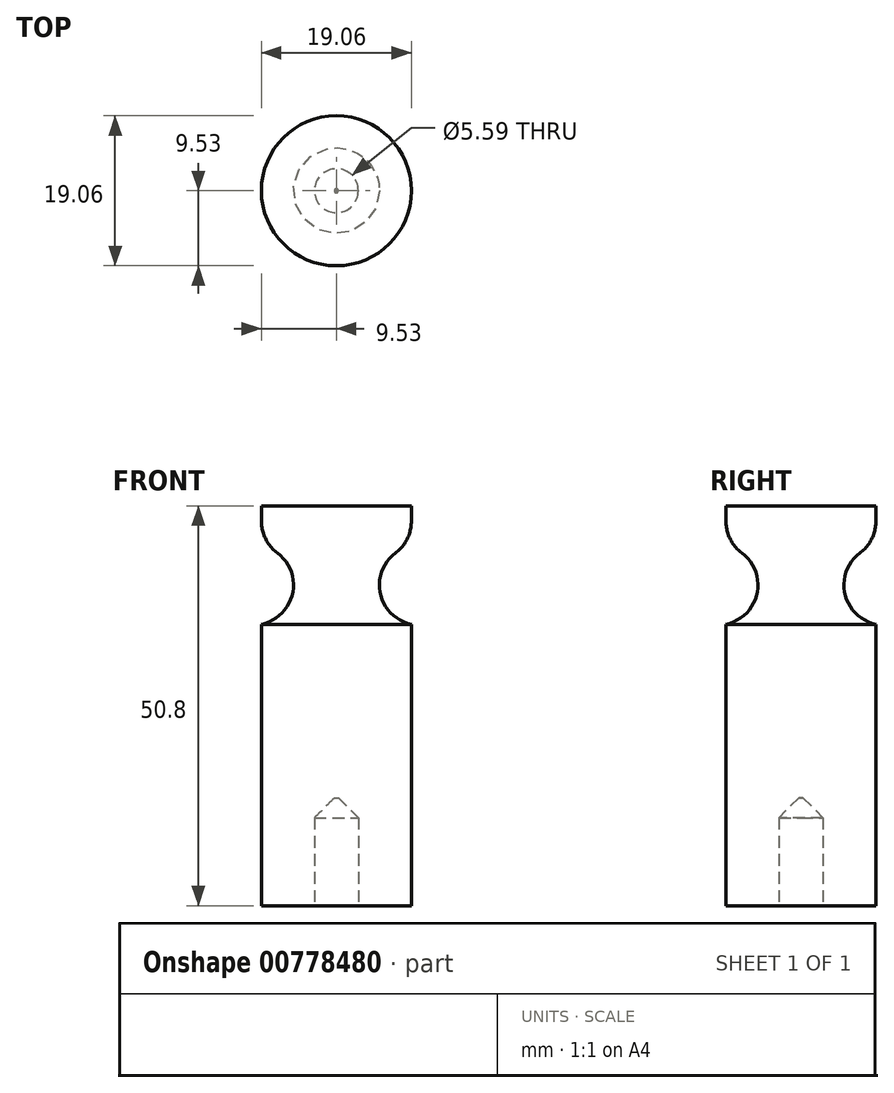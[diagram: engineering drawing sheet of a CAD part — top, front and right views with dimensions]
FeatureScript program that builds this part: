
annotation { "Feature Type Name" : "Feature", "Feature Type Description" : "" }
export const myFeature = defineFeature(function(context is Context, id is Id, definition is map)
    precondition{}
    {
        {
            var Q0;
            Q0=qCreatedBy(makeId("Top.planeOp"),FACE);
            var sketch = newSketch(context, id + "F0", { "sketchPlane" : qUnion([Q0])});
            skCircle(sketch, "E0", {"center": v(0, 0) * mm, "radius": 9.53 * mm});
            skSolve(sketch);
        }
        {
            var Q0;
            Q0 = qSketchRegion(id + "F0", true);
            extrude(context, id + "F1", {"entities" : qUnion([Q0]), "depth" : 50.8 * mm, "offsetDistance" : 25.4 * mm});
        }
        {
            var Q0;
            Q0=qCreatedBy(makeId("Front.planeOp"),FACE);
            var sketch = newSketch(context, id + "F2", { "sketchPlane" : qUnion([Q0])});
            skArc(sketch, "E1", {"start": v(9.52, 45.72) * mm, "mid": v(5.46, 40.74) * mm, "end": v(9.53, 35.76) * mm});
            skLineSegment(sketch, "E2", {"start": v(9.52, 45.72) * mm, "end": v(9.53, 35.76) * mm});
            skLineSegment(sketch, "E3", {"start": v(0, 50.97) * mm, "end": v(0, -98.87) * mm});
            skSolve(sketch);
        }
        {
            var Q0;
            Q0 = qSketchRegion(id + "F2", true);
            var Q1;
            Q1=sQuery(id+"F2.wireOp",EDGE,"E3");
            revolve(context, id + "F3", {"operationType" : NewBodyOperationType.REMOVE, "surfaceOperationType" : NewSurfaceOperationType.NEW, "entities" : qUnion([Q0]), "axis" : qUnion([Q1]), "revolveType" : RevolveType.FULL});
        }
        {
            var Q0;
            {var subQ0=sQuery(id+"F2.wireOp",EDGE,"E2");var subQ1=sQuery(id+"F2.wireOp",EDGE,"E1");Q0=makeQuery(id+"F3.boolean.opBoolean","COPY",EDGE,{"derivedFrom":makeQuery(id+"F3.opRevolve","SWEPT_EDGE",EDGE,{"disambiguationData":[OSD([subQ1,subQ0]),TDD([makeQuery(id+"F2.imprint","INTERSECT",VERTEX,{"disambiguationData":[OD(0.0)],"derivedFrom":[subQ1,subQ0]})])]})});}
            var Q1;
            {var subQ0=sQuery(id+"F2.wireOp",EDGE,"E2");var subQ1=sQuery(id+"F2.wireOp",EDGE,"E1");Q1=makeQuery(id+"F3.boolean.opBoolean","COPY",EDGE,{"derivedFrom":makeQuery(id+"F3.opRevolve","SWEPT_EDGE",EDGE,{"disambiguationData":[OSD([subQ1,subQ0]),TDD([makeQuery(id+"F2.imprint","INTERSECT",VERTEX,{"disambiguationData":[OD(1.0)],"derivedFrom":[subQ1,subQ0]})])]})});}
            fillet(context, id + "F4", {"entities" : qUnion([Q0, Q1]), "radius" : 5.08 * mm, "tangentPropagation" : true, "allowEdgeOverflow" : false});
        }
        {
            var Q0;
            Q0=makeQuery(id+"F1.opExtrude","CAP_FACE",FACE,{"disambiguationData":[OSD([sQuery(id+"F0.wireOp",EDGE,"E0")])],"isStart":true});
            var sketch = newSketch(context, id + "F5", { "sketchPlane" : qUnion([Q0])});
            skCircle(sketch, "E4", {"center": v(0, 0) * mm, "radius": 2.8 * mm});
            skSolve(sketch);
        }
        {
            var Q0;
            Q0 = qSketchRegion(id + "F5", true);
            extrude(context, id + "F6", {"entities" : qUnion([Q0]), "operationType" : NewBodyOperationType.REMOVE, "oppositeDirection" : true, "depth" : 13.72 * mm, "offsetDistance" : 25.4 * mm});
        }
        {
            var Q0;
            Q0=makeQuery(id+"F6.boolean.opBoolean","COPY",EDGE,{"derivedFrom":makeQuery(id+"F6.opExtrude","CAP_EDGE",EDGE,{"disambiguationData":[OSD([sQuery(id+"F5.wireOp",EDGE,"E4")])],"isStart":false})});
            chamfer(context, id + "F7", {"entities" : qUnion([Q0]), "width" : 2.54 * mm, "tangentPropagation" : true});
        }
    });
